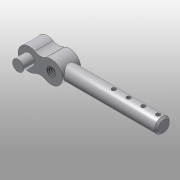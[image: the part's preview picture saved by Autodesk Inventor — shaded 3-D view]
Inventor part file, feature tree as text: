
AUTODESK INVENTOR PART (.ipt)
format: ipt  version: 2016 (Build 200138000, 138)  size: 136,704 bytes
history: native  units: mm
features: extrude x4, sketch x4, hole x1, pattern_linear x1, chamfer x1, projected_geometry x1
ambient origin geometry x8: Origin, YZ Plane, XZ Plane, XY Plane, X Axis, Y Axis, Z Axis, Center Point
bodies: Solid1 (feature_tree)
feature tree (12):
  extrude  "Extrusion1"  Depth=6.0mm
  extrude  "Extrusion2"  Depth=3.0mm
  extrude  "Extrusion3"  Depth=6.0mm
  hole  "Hole1"  [1 undecoded]
  extrude  "Extrusion4"  Depth=31.0mm TaperAngle=0.0deg
  pattern_linear  "Rectangular Pattern1"  Spacing1=3.0mm  [1 undecoded]
  chamfer  "Chamfer1"  Distance=3.0mm
  sketch  "Sketch1"  dims[d0=6.0mm d1=6.0mm]
  sketch  "Sketch2"  dims[d2=6.0mm d3=3.0mm]
  sketch  "Sketch3"  dims[d4=6.0mm d5=6.0mm]
  sketch  "Sketch4"  dims[d6=5.0mm d7=0.0mm d8=4.0mm d9=31.0mm d10=0.0mm d11=3.0mm d12=3.0mm d13=0.0mm d14=10.0mm d15=10.0mm d16=2.459mm d17=6.0mm d18=4.0mm d19=2.0mm d20=90.0deg d21=8.8mm d22=20.594885mm d23=1.1mm d24=1.5mm d25=17.5mm d26=0.0mm d27=40.0mm d29=4.0mm d30=0.5mm d31=2.0mm d32=45.0deg]
  projected_geometry  "Project Cut Edges1"
note: 2 required parameter values undecoded (feature->parameter linkage not recoverable at this tier; creation-order binding heuristic only, values carry confidence <= 0.55)
